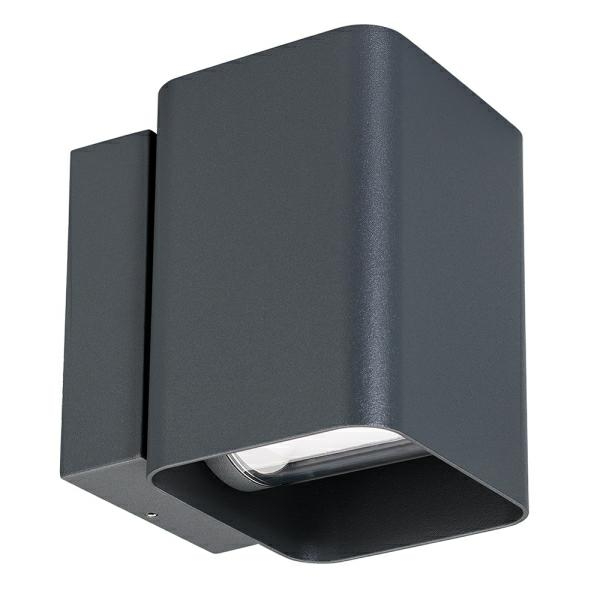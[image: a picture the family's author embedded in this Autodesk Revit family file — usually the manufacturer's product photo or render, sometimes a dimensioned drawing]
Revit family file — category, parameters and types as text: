
# Revit family: VARIO
name_source: partatom
category: Осветительные приборы
revit_build: Autodesk Revit 2017 (Build: 20160225_1515(x64)
units: mm (PartAtom-declared; Revit-internal decimal feet)

## family parameters
Всегда вертикально = Да
Источник света = Да
На основе рабочей плоскости = Нет
Общий = Нет
При загрузке вырезать с полостями = Нет
Размер круглого соединителя = Использовать диаметр
Тип детали = Нормальный
Точка расчета площади = Нет

## types (5) — shared parameters
ADSK_Единица измерения = шт.
ADSK_Завод-изготовитель = ARLIGHT
ADSK_Классификация нагрузок = Освещение
ADSK_Количество фаз = 1
ADSK_Количество фаз числовое = 1
ADSK_Коэффициент мощности = 0.5
ADSK_Наименование = Светильник
ADSK_Напряжение = 220 В
ADSK_Номинальная мощность = 12 Вт
ADSK_Полная мощность = 24 В·А
ADSK_Размер_Высота = 132 мм
ADSK_Размер_Длина = 129 мм
ADSK_Размер_Ширина = 104 мм
ADSK_Ток = 0 А
ARL_Драйвер = Встроенный
ARL_Индекс цветопередачи = >80
ARL_Класс защиты от поражения электрическим током = II
ARL_Класс пылевлагозащиты = IP54
ARL_Рабочая температура окружающей среды = -40...+40 °C
ARL_Серия = VARIO
ARL_Способ монтажа = Накладной
ARL_Тип товара = Светильник
ARL_Угол обзора = 80°
URL = https://arlight.ru
Видимая форма излучения при визуализации = Нет
Группа модели = Светильники
Изготовитель = ARLIGHT
Излучение по длине прямоугольника = 100 мм
Излучение по ширине прямоугольника = 31 мм
Полная установленная мощность = 24 В·А
Разработчик = НТЦ Конструктор
Разработчик (URL) = https://constructor.ru
Разработчик (телефон) = +7 (495) 781-05-35
Светофильтр = 16777215
Смещение цветовой температуры при затухании лампы = <Нет>
Угол наклона = 90.00°

## per-type parameters (varying)
| type | ADSK_Код изделия | ADSK_Марка | ADSK_Масса_Текст | ARL_Материал корпуса | ARL_Область использования | ARL_Обозначение корпуса | ARL_Цвет покрытия | ARL_Цвет свечения | Комментарии к типоразмеру | Описание | Файл фотометрической сетки |
| 024391 Светильник LGD-Wall-Vario-J2WH-12W Warm White | Арт. 024391 | LGD-Wall-Vario-J2WH-12W Warm White | 1.1 | Металл, белый | Для ландшафтного освещения придомовых территорий, декоративной подсветки фасадов | Корпус прямоугольный, алюминий, цвет темно-коричневый | Белый | Теплый 3000K | Арт. 024391 | Уличный светодиодный светильник для стен, изменяемый угол освещения 0°-80°, свет вверх-вниз на 2 стороны. Цвет ТЕПЛЫЙ БЕЛЫЙ 3000К, светодиоды 2x6 Вт CREE (750 лм). Влагозащищенный корпус IP54 - белый алюминий, экран ударопрочный PC. Питание 220 В, мощность 12 Вт. Размеры ВхШхГ -138х104х129 мм | 024391_LGD-Wall-Vario-J2WH-12W Warm White.ies |
| 022002 Светильник LGD-Wall-Vario-J2R-12W Warm White | Арт. 022002 | LGD-Wall-Vario-J2R-12W Warm White | 1.145 | Металл, темно-коричневый | Для ландшафтного освещения придомовых территорий, декоративной подсветки фасадов | Корпус прямоугольный, алюминий, цвет темно-коричневый | Темно-коричневый | Теплый 3000K | Арт. 022002 | Уличный светодиодный светильник для стен, изменяемый угол освещения 0°-80°, свет вверх-вниз на 2 стороны. Цвет ТЕПЛЫЙ БЕЛЫЙ 3000К, светодиоды 2x6 Вт CREE (750 лм). Влагозащищенный корпус IP54 - терракотовый алюминий, экран ударопрочный PC. Питание 220 В, мощность 12 Вт. Размеры ВхШхГ -138х104х129 мм | 022002_LGD-Wall-Vario-J2R-12W Warm White.ies |
| 029794 Светильник LGD-WALL-VARIO-S104x129-2x6W Day4000 | Арт. 029794 | LGD-WALL-VARIO-S104x129-2x6W Day4000 | 1 | Металл, темно-серый | Категория размещения - 4 | Корпус прямоугольный, алюминий, цвет темно-серый | Темно-серый | Дневной 4000K | Арт. 029794 | Светильник LGD-WALL-VARIO-S104x129-2x6W Day4000 (GR, 1-80 deg) (ARL, IP54 Металл, 3 года) | 029794_LGD-WALL-VARIO-S104x129-2x6W Day4000 (GR, 1-80 deg).ies |
| 021933 Светильник LGD-Wall-Vario-J2G-12W Warm White | Арт. 021933 | LGD-Wall-Vario-J2G-12W Warm White | 1.145 | Металл, темно-серый | Для ландшафтного освещения придомовых территорий, декоративной подсветки фасадов | Корпус прямоугольный, алюминий, цвет темно-серый | Темно-серый | Теплый 3000K | Арт. 021933 | Уличный светодиодный светильник для стен, изменяемый угол освещения 0°-80°, свет вверх-вниз на 2 стороны. Цвет ТЕПЛЫЙ БЕЛЫЙ 3000К, светодиоды 2x6 Вт CREE (750 лм). Влагозащищенный корпус IP54 - темно-серый алюминий, экран ударопрочный PC. Питание 220 В, мощность 12 Вт. Размеры ВхШхГ -138х104х129 мм | 021933_LGD-Wall-Vario-J2G-12W Warm White.ies |
| 021932 Светильник LGD-Wall-Vario-J2B-12W Warm White | Арт. 021932 | LGD-Wall-Vario-J2B-12W Warm White | 1.145 | Металл, чёрный | Для ландшафтного освещения придомовых территорий, декоративной подсветки фасадов | Корпус прямоугольный, алюминий, цвет черный | Черный | Теплый 3000K | Арт. 021932 | Уличный светодиодный светильник для стен, изменяемый угол освещения 0°-80°, свет вверх-вниз на 2 стороны. Цвет ТЕПЛЫЙ БЕЛЫЙ 3000К, светодиоды 2x6 Вт CREE (750 лм). Влагозащищенный корпус IP54 - черный алюминий, экран ударопрочный PC. Питание 220 В, мощность 12 Вт. Размеры ВхШхГ -138х104х129 мм | 021932_LGD-Wall-Vario-J2B-12W Warm White.ies |
